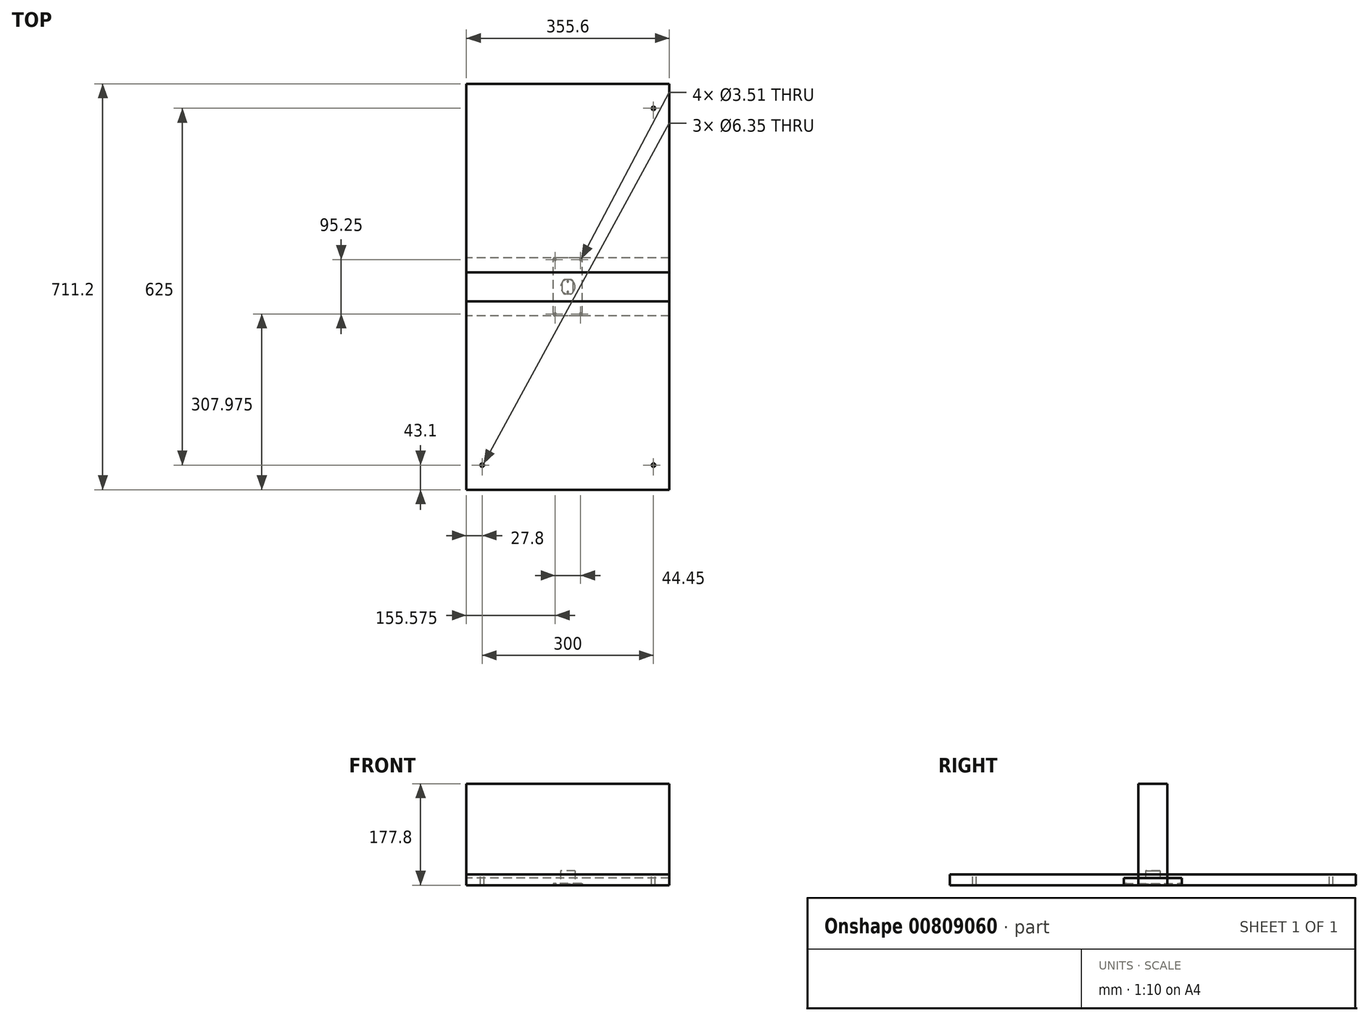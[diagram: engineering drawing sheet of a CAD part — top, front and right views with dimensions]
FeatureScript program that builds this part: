
annotation { "Feature Type Name" : "Feature", "Feature Type Description" : "" }
export const myFeature = defineFeature(function(context is Context, id is Id, definition is map)
    precondition{}
    {
        {
            var Q0;
            Q0=qCreatedBy(makeId("Top.planeOp"),FACE);
            var sketch = newSketch(context, id + "F0", { "sketchPlane" : qUnion([Q0])});
            skLineSegment(sketch, "E0.bottom", {"start": v(177.8, -355.6) * mm, "end": v(-177.8, -355.6) * mm});
            skLineSegment(sketch, "E0.top", {"start": v(177.8, 355.6) * mm, "end": v(-177.8, 355.6) * mm});
            skLineSegment(sketch, "E0.left", {"start": v(177.8, -355.6) * mm, "end": v(177.8, 355.6) * mm});
            skLineSegment(sketch, "E0.right", {"start": v(-177.8, -355.6) * mm, "end": v(-177.8, 355.6) * mm});
            skPoint(sketch, "E0.middle", {"position": v(0, 0) * mm});
            skSolve(sketch);
        }
        {
            var Q0;
            Q0 = qSketchRegion(id + "F0", true);
            extrude(context, id + "F1", {"entities" : qUnion([Q0]), "depth" : 19.05 * mm, "offsetDistance" : 25.4 * mm});
        }
        {
            var Q0;
            Q0=qCreatedBy(makeId("Top.planeOp"),FACE);
            var sketch = newSketch(context, id + "F2", { "sketchPlane" : qUnion([Q0])});
            skLineSegment(sketch, "E1.bottom", {"start": v(177.8, -25.4) * mm, "end": v(-177.8, -25.4) * mm});
            skLineSegment(sketch, "E1.top", {"start": v(177.8, 25.4) * mm, "end": v(-177.8, 25.4) * mm});
            skLineSegment(sketch, "E1.left", {"start": v(177.8, -25.4) * mm, "end": v(177.8, 25.4) * mm});
            skLineSegment(sketch, "E1.right", {"start": v(-177.8, -25.4) * mm, "end": v(-177.8, 25.4) * mm});
            skPoint(sketch, "E1.middle", {"position": v(0, 0) * mm});
            skSolve(sketch);
        }
        {
            var Q0;
            Q0 = qSketchRegion(id + "F2", true);
            extrude(context, id + "F3", {"entities" : qUnion([Q0]), "depth" : 177.8 * mm, "offsetDistance" : 25.4 * mm});
        }
        {
            var Q0;
            Q0=qCreatedBy(makeId("Top.planeOp"),FACE);
            var sketch = newSketch(context, id + "F4", { "sketchPlane" : qUnion([Q0])});
            skLineSegment(sketch, "E2.bottom", {"start": v(177.8, -50.8) * mm, "end": v(-177.8, -50.8) * mm});
            skLineSegment(sketch, "E2.top", {"start": v(177.8, 50.8) * mm, "end": v(-177.8, 50.8) * mm});
            skLineSegment(sketch, "E2.left", {"start": v(177.8, -50.8) * mm, "end": v(177.8, 50.8) * mm});
            skLineSegment(sketch, "E2.right", {"start": v(-177.8, -50.8) * mm, "end": v(-177.8, 50.8) * mm});
            skPoint(sketch, "E2.middle", {"position": v(0, 0) * mm});
            skSolve(sketch);
        }
        {
            var Q0;
            Q0 = qSketchRegion(id + "F4", true);
            extrude(context, id + "F5", {"entities" : qUnion([Q0]), "depth" : 12.7 * mm, "offsetDistance" : 25.4 * mm});
        }
        {
            var Q0;
            Q0=qCreatedBy(makeId("Top.planeOp"),FACE);
            var sketch = newSketch(context, id + "F6", { "sketchPlane" : qUnion([Q0])});
            skCircle(sketch, "E3", {"center": v(0, 0) * mm, "radius": 12.7 * mm});
            skSolve(sketch);
        }
        {
            var Q0;
            Q0 = qSketchRegion(id + "F6", true);
            extrude(context, id + "F7", {"entities" : qUnion([Q0]), "depth" : 25.4 * mm, "offsetDistance" : 25.4 * mm});
        }
        {
            var Q0;
            Q0=makeQuery(id+"F1.opExtrude","CAP_FACE",FACE,{"disambiguationData":[OSD([sQuery(id+"F0.wireOp",EDGE,"E0.bottom"),sQuery(id+"F0.wireOp",EDGE,"E0.top"),sQuery(id+"F0.wireOp",EDGE,"E0.left"),sQuery(id+"F0.wireOp",EDGE,"E0.right")])],"isStart":false});
            var sketch = newSketch(context, id + "F8", { "sketchPlane" : qUnion([Q0])});
            skLineSegment(sketch, "E4.bottom", {"start": v(150, 312.5) * mm, "end": v(-150, 312.5) * mm, "construction": true});
            skLineSegment(sketch, "E4.top", {"start": v(150, -312.5) * mm, "end": v(-150, -312.5) * mm, "construction": true});
            skLineSegment(sketch, "E4.left", {"start": v(150, 312.5) * mm, "end": v(150, -312.5) * mm, "construction": true});
            skLineSegment(sketch, "E4.right", {"start": v(-150, 312.5) * mm, "end": v(-150, -312.5) * mm, "construction": true});
            skPoint(sketch, "E4.middle", {"position": v(0, 0) * mm});
            skSolve(sketch);
        }
        {
            var Q0;
            Q0=sQuery(id+"F8.wireOp",VERTEX,"E4.top.end");
            var Q1;
            Q1=sQuery(id+"F8.wireOp",VERTEX,"E4.top.start");
            var Q2;
            Q2=sQuery(id+"F8.wireOp",VERTEX,"E4.bottom.start");
            var Q3;
            Q3=makeQuery(id+"F1.opExtrude","SWEPT_BODY",BODY,{"disambiguationData":[OSD([sQuery(id+"F0.wireOp",EDGE,"E0.bottom"),sQuery(id+"F0.wireOp",EDGE,"E0.top"),sQuery(id+"F0.wireOp",EDGE,"E0.left"),sQuery(id+"F0.wireOp",EDGE,"E0.right")])]});
            hole(context, id + "F9", {"style" : HoleStyle.SIMPLE, "endStyle" : HoleEndStyle.THROUGH, "holeDiameter" : 6.35 * mm, "majorDiameter" : 6.35 * mm, "isTappedThrough" : true, "tappedDepth" : 12.7 * mm, "tapClearance" : 3, "locations" : qUnion([Q0, Q1, Q2]), "scope" : qUnion([Q3])});
        }
        {
            var Q0;
            Q0 = qSketchRegion(id + "F0", true);
            var sketch = newSketch(context, id + "F10", { "sketchPlane" : qUnion([Q0])});
            skLineSegment(sketch, "E5.bottom", {"start": v(25.4, -50.8) * mm, "end": v(-25.4, -50.8) * mm});
            skLineSegment(sketch, "E5.top", {"start": v(25.4, 50.8) * mm, "end": v(-25.4, 50.8) * mm});
            skLineSegment(sketch, "E5.left", {"start": v(25.4, -50.8) * mm, "end": v(25.4, 50.8) * mm});
            skLineSegment(sketch, "E5.right", {"start": v(-25.4, -50.8) * mm, "end": v(-25.4, 50.8) * mm});
            skPoint(sketch, "E5.middle", {"position": v(0, 0) * mm});
            skSolve(sketch);
        }
        {
            var Q0;
            Q0 = qSketchRegion(id + "F10", true);
            extrude(context, id + "F11", {"entities" : qUnion([Q0]), "depth" : 3.17 * mm, "offsetDistance" : 25.4 * mm});
        }
        {
            var Q0;
            Q0=makeQuery(id+"F11.opExtrude","SWEPT_EDGE",EDGE,{"disambiguationData":[OSD([sQuery(id+"F10.wireOp",EDGE,"E5.bottom"),sQuery(id+"F10.wireOp",EDGE,"E5.left")])]});
            var Q1;
            Q1=makeQuery(id+"F11.opExtrude","SWEPT_EDGE",EDGE,{"disambiguationData":[OSD([sQuery(id+"F10.wireOp",EDGE,"E5.bottom"),sQuery(id+"F10.wireOp",EDGE,"E5.right")])]});
            var Q2;
            Q2=makeQuery(id+"F11.opExtrude","SWEPT_EDGE",EDGE,{"disambiguationData":[OSD([sQuery(id+"F10.wireOp",EDGE,"E5.top"),sQuery(id+"F10.wireOp",EDGE,"E5.left")])]});
            var Q3;
            Q3=makeQuery(id+"F11.opExtrude","SWEPT_EDGE",EDGE,{"disambiguationData":[OSD([sQuery(id+"F10.wireOp",EDGE,"E5.top"),sQuery(id+"F10.wireOp",EDGE,"E5.right")])]});
            fillet(context, id + "F12", {"entities" : qUnion([Q0, Q1, Q2, Q3]), "radius" : 1.59 * mm, "tangentPropagation" : true, "allowEdgeOverflow" : false});
        }
        {
            var Q0;
            Q0=makeQuery(id+"F11.opExtrude","CAP_FACE",FACE,{"disambiguationData":[OSD([sQuery(id+"F10.wireOp",EDGE,"E5.bottom"),sQuery(id+"F10.wireOp",EDGE,"E5.top"),sQuery(id+"F10.wireOp",EDGE,"E5.left"),sQuery(id+"F10.wireOp",EDGE,"E5.right")])],"isStart":false});
            var sketch = newSketch(context, id + "F13", { "sketchPlane" : qUnion([Q0])});
            skLineSegment(sketch, "E6.bottom", {"start": v(-22.23, -47.62) * mm, "end": v(22.23, -47.62) * mm});
            skLineSegment(sketch, "E6.top", {"start": v(-22.23, 47.62) * mm, "end": v(22.23, 47.62) * mm});
            skLineSegment(sketch, "E6.left", {"start": v(-22.23, -47.62) * mm, "end": v(-22.23, 47.62) * mm});
            skLineSegment(sketch, "E6.right", {"start": v(22.23, -47.62) * mm, "end": v(22.23, 47.62) * mm});
            skPoint(sketch, "E6.middle", {"position": v(0, 0) * mm});
            skSolve(sketch);
        }
        {
            var Q0;
            Q0=sQuery(id+"F13.wireOp",VERTEX,"E6.bottom.end");
            var Q1;
            Q1=sQuery(id+"F13.wireOp",VERTEX,"E6.bottom.start");
            var Q2;
            Q2=sQuery(id+"F13.wireOp",VERTEX,"E6.left.end");
            var Q3;
            Q3=sQuery(id+"F13.wireOp",VERTEX,"E6.top.end");
            var Q4;
            Q4=makeQuery(id+"F11.opExtrude","SWEPT_BODY",BODY,{"disambiguationData":[OSD([sQuery(id+"F10.wireOp",EDGE,"E5.bottom"),sQuery(id+"F10.wireOp",EDGE,"E5.top"),sQuery(id+"F10.wireOp",EDGE,"E5.left"),sQuery(id+"F10.wireOp",EDGE,"E5.right")])]});
            hole(context, id + "F14", {"style" : HoleStyle.SIMPLE, "endStyle" : HoleEndStyle.THROUGH, "holeDiameter" : 3.5 * mm, "majorDiameter" : 6.35 * mm, "isTappedThrough" : true, "tappedDepth" : 12.7 * mm, "tapClearance" : 3, "locations" : qUnion([Q0, Q1, Q2, Q3]), "scope" : qUnion([Q4])});
        }
        {
            var Q0;
            Q0=qCreatedBy(makeId("Top.planeOp"),FACE);
            var sketch = newSketch(context, id + "F15", { "sketchPlane" : qUnion([Q0])});
            skLineSegment(sketch, "E7.bottom", {"start": v(9.53, -12.7) * mm, "end": v(-9.52, -12.7) * mm});
            skLineSegment(sketch, "E7.top", {"start": v(9.52, 12.7) * mm, "end": v(-9.53, 12.7) * mm});
            skLineSegment(sketch, "E7.left", {"start": v(9.53, -12.7) * mm, "end": v(9.52, 12.7) * mm});
            skLineSegment(sketch, "E7.right", {"start": v(-9.52, -12.7) * mm, "end": v(-9.53, 12.7) * mm});
            skPoint(sketch, "E7.middle", {"position": v(0, 0) * mm});
            skSolve(sketch);
        }
        {
            var Q0;
            Q0 = qSketchRegion(id + "F15", true);
            extrude(context, id + "F16", {"entities" : qUnion([Q0]), "depth" : 1.59 * mm, "offsetDistance" : 25.4 * mm});
        }
        {
            var Q0;
            Q0=makeQuery(id+"F16.opExtrude","SWEPT_EDGE",EDGE,{"disambiguationData":[OSD([sQuery(id+"F15.wireOp",EDGE,"E7.bottom"),sQuery(id+"F15.wireOp",EDGE,"E7.left")])]});
            var Q1;
            Q1=makeQuery(id+"F16.opExtrude","SWEPT_EDGE",EDGE,{"disambiguationData":[OSD([sQuery(id+"F15.wireOp",EDGE,"E7.bottom"),sQuery(id+"F15.wireOp",EDGE,"E7.right")])]});
            var Q2;
            Q2=makeQuery(id+"F16.opExtrude","SWEPT_EDGE",EDGE,{"disambiguationData":[OSD([sQuery(id+"F15.wireOp",EDGE,"E7.top"),sQuery(id+"F15.wireOp",EDGE,"E7.left")])]});
            var Q3;
            Q3=makeQuery(id+"F16.opExtrude","SWEPT_EDGE",EDGE,{"disambiguationData":[OSD([sQuery(id+"F15.wireOp",EDGE,"E7.top"),sQuery(id+"F15.wireOp",EDGE,"E7.right")])]});
            fillet(context, id + "F17", {"entities" : qUnion([Q0, Q1, Q2, Q3]), "radius" : 5.08 * mm, "tangentPropagation" : true, "allowEdgeOverflow" : false});
        }
        {
            var Q0;
            Q0=makeQuery(id+"F16.opExtrude","CAP_FACE",FACE,{"disambiguationData":[OSD([sQuery(id+"F15.wireOp",EDGE,"E7.bottom"),sQuery(id+"F15.wireOp",EDGE,"E7.top"),sQuery(id+"F15.wireOp",EDGE,"E7.left"),sQuery(id+"F15.wireOp",EDGE,"E7.right")])],"isStart":false});
            var sketch = newSketch(context, id + "F18", { "sketchPlane" : qUnion([Q0])});
            skLineSegment(sketch, "E8.bottom", {"start": v(6.35, -9.53) * mm, "end": v(-6.35, -9.53) * mm});
            skLineSegment(sketch, "E8.top", {"start": v(6.35, 9.53) * mm, "end": v(-6.35, 9.53) * mm});
            skLineSegment(sketch, "E8.left", {"start": v(6.35, -9.53) * mm, "end": v(6.35, 9.53) * mm});
            skLineSegment(sketch, "E8.right", {"start": v(-6.35, -9.53) * mm, "end": v(-6.35, 9.53) * mm});
            skPoint(sketch, "E8.middle", {"position": v(0, 0) * mm});
            skPoint(sketch, "E9", {"position": v(-6.35, 0) * mm});
            skPoint(sketch, "E10", {"position": v(6.35, 0) * mm});
            skPoint(sketch, "E11", {"position": v(0, 9.53) * mm});
            skPoint(sketch, "E12", {"position": v(0, -9.53) * mm});
            skSolve(sketch);
        }
        {
            var Q0;
            Q0=sQuery(id+"F18.wireOp",VERTEX,"E11");
            var Q1;
            Q1=sQuery(id+"F18.wireOp",VERTEX,"E12");
            var Q2;
            Q2=makeQuery(id+"F16.opExtrude","SWEPT_BODY",BODY,{"disambiguationData":[OSD([sQuery(id+"F15.wireOp",EDGE,"E7.bottom"),sQuery(id+"F15.wireOp",EDGE,"E7.top"),sQuery(id+"F15.wireOp",EDGE,"E7.left"),sQuery(id+"F15.wireOp",EDGE,"E7.right")])]});
            hole(context, id + "F19", {"style" : HoleStyle.SIMPLE, "endStyle" : HoleEndStyle.THROUGH, "holeDiameter" : 2.84 * mm, "majorDiameter" : 6.35 * mm, "isTappedThrough" : true, "tappedDepth" : 12.7 * mm, "tapClearance" : 3, "locations" : qUnion([Q0, Q1]), "scope" : qUnion([Q2])});
        }
    });
